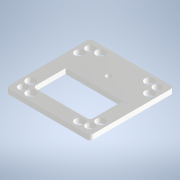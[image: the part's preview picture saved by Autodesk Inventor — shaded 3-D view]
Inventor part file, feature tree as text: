
AUTODESK INVENTOR PART (.ipt)
format: ipt  version: 2022 (Build 260153000, 153)  size: 232,960 bytes
history: native  units: mm
features: reference x3, other x3, extrude x2, mirror x2, sketch x1, projected_geometry x1
ambient origin geometry x8: Origin, YZ Plane, XZ Plane, XY Plane, X Axis, Y Axis, Z Axis, Center Point
bodies: Volumenkörper1 (feature_tree)
feature tree (12):
  extrude  "Extrusion1"  TaperAngle=0.0deg  [1 undecoded]
  mirror  "Mirror6"
  mirror  "Mirror7"
  extrude  "Extrusion17"  TaperAngle=0.0deg  [1 undecoded]
  sketch  "Sketch32"  dims[d5=0.0mm d6=0.0mm d7=0.0mm d8=0.0mm d9=0.0mm d13=0.0mm d14=0.0mm d20=0.0mm d21=0.0mm d22=0.0mm d23=0.0mm d24=0.0mm d25=3.0mm d26=0.0mm d27=0.0mm d28=0.0mm d29=0.0mm d30=0.0mm d31=0.0mm d32=0.0mm d33=0.0mm d34=0.0mm d46=0.0mm d47=0.0mm d48=0.0mm d49=-10.0mm d50=0.0mm d51=0.0mm d52=0.0mm d53=0.0mm d54=0.0mm d55=0.0mm d56=0.0mm d57=0.0mm d58=0.0mm d59=0.0mm d77=2.65mm d82=2.65mm d222=0.5mm d236=5.3mm d278=25.0mm d279=25.0mm d2=8.0mm d281=8.0mm d282=2.0mm d283=4.85mm d284=20.0mm d4=20.0mm d286=5.3mm d290=20.8mm d292=2.0mm d313=6.3mm d314=6.3mm d330=0.0mm d331=0.0mm d332=0.0mm d354=3.0mm d355=3.0mm d356=0.0mm]
  reference  "Reference9"
  reference  "Reference10"
  reference  "Reference11"
  projected_geometry  "Projected Loop27"
  other  "Assembly_Cube_Z_Focus_MGN_NEMA_v3.iam"
  other  "00_Motorcoupling_5mm_M3:1"
  other  "30_Cube_Z_Focus_Drylin_NEMA_slide_part1:1"
note: 2 required parameter values undecoded (feature->parameter linkage not recoverable at this tier; creation-order binding heuristic only, values carry confidence <= 0.55)
